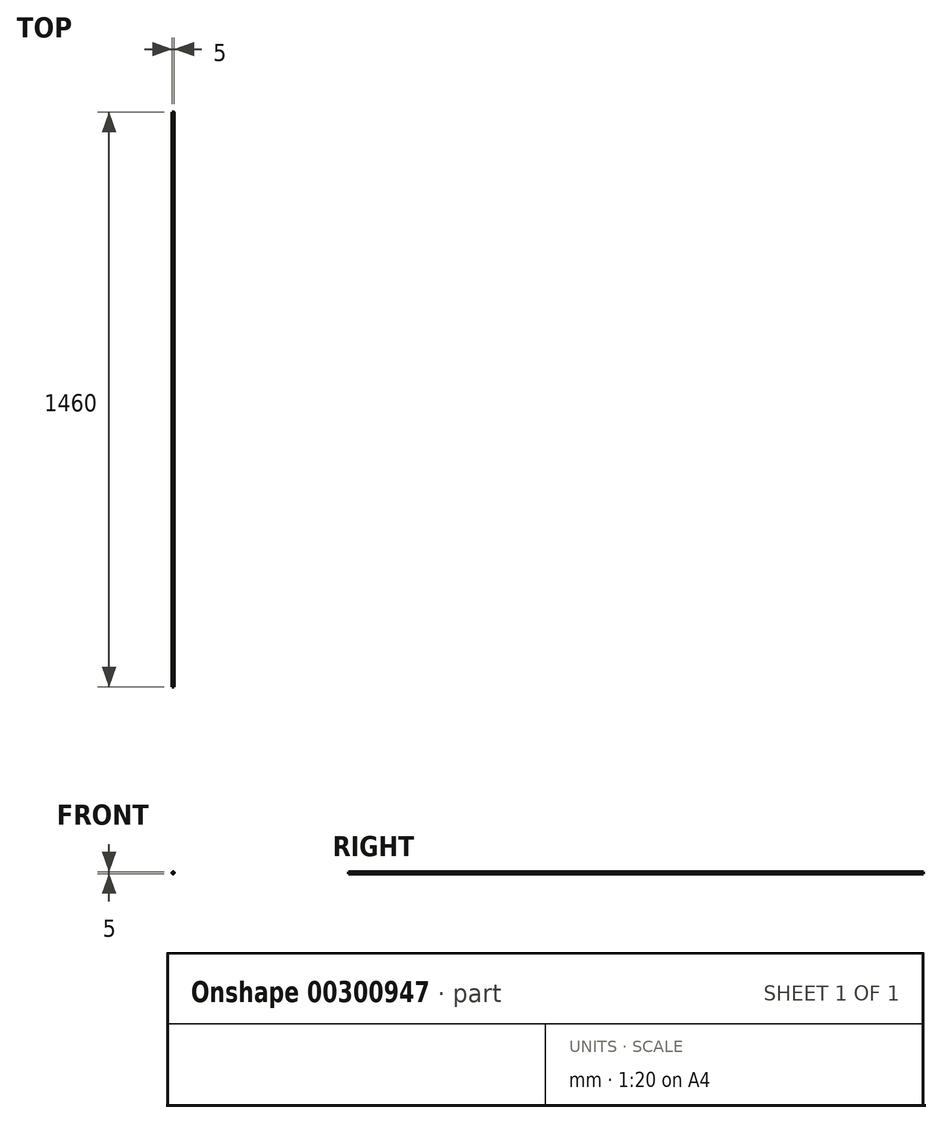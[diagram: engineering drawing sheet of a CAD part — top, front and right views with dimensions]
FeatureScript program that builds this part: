
annotation { "Feature Type Name" : "Feature", "Feature Type Description" : "" }
export const myFeature = defineFeature(function(context is Context, id is Id, definition is map)
    precondition{}
    {
        {
            var Q0;
            Q0=qCreatedBy(makeId("Front.planeOp"),FACE);
            var sketch = newSketch(context, id + "F0", { "sketchPlane" : qUnion([Q0])});
            skCircle(sketch, "E0", {"center": v(0, 0) * mm, "radius": 2.5 * mm});
            skSolve(sketch);
        }
        {
            var Q0;
            Q0=makeQuery(id+"F0.imprint","IMPRINT",FACE,{"disambiguationData":[TD([[makeQuery(id+"F0.imprint","IMPRINT",EDGE,{"derivedFrom":sQuery(id+"F0.wireOp",EDGE,"E0")}),1.0]])]});
            extrude(context, id + "F1", {"entities" : qUnion([Q0]), "depth" : 1460 * mm});
        }
    });
